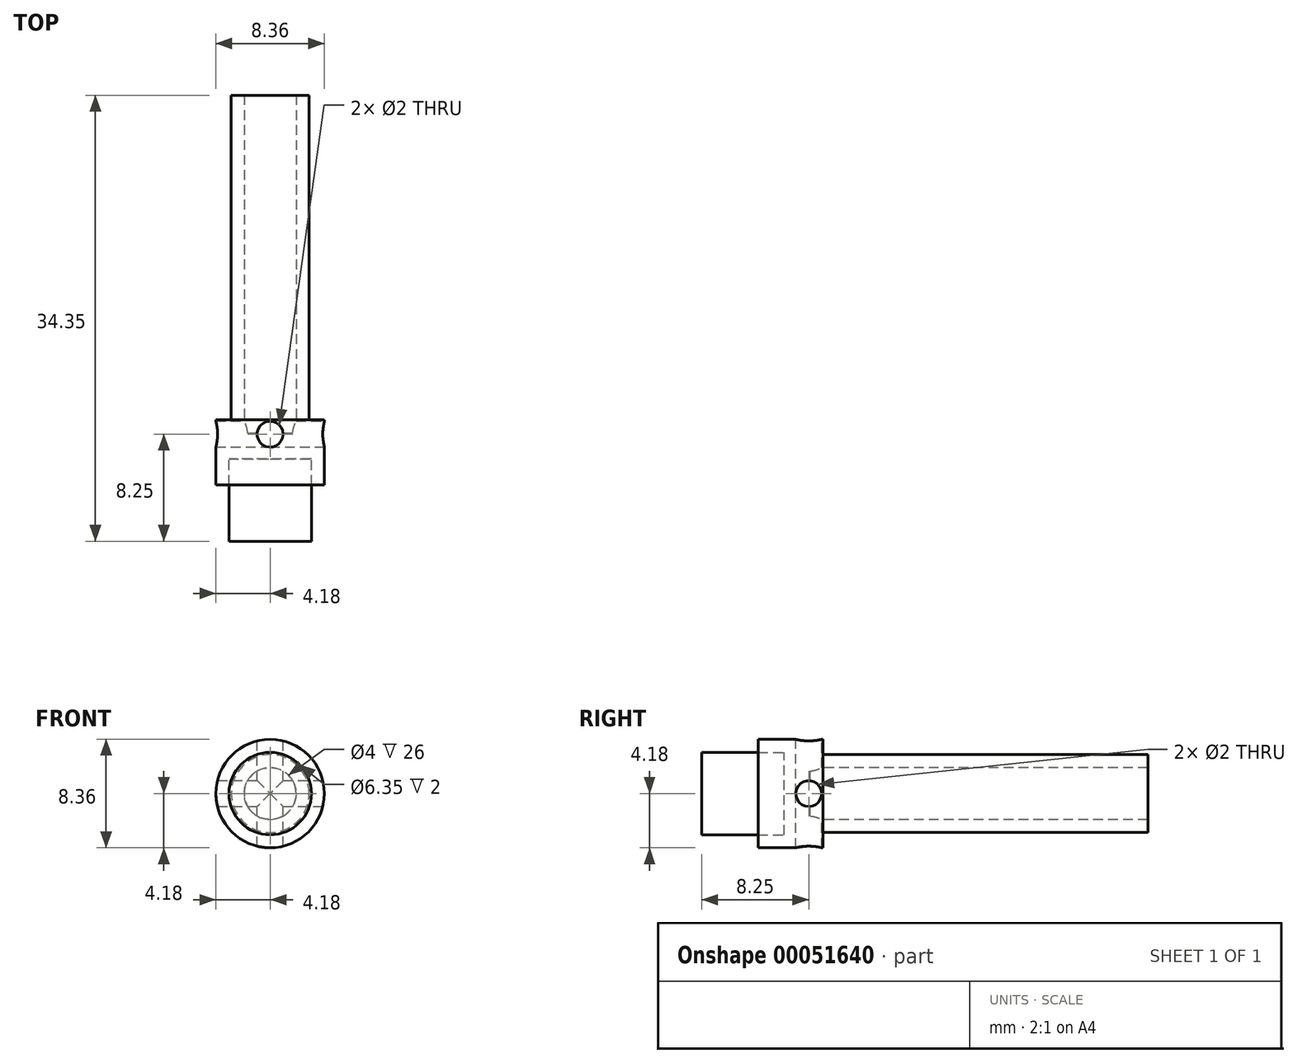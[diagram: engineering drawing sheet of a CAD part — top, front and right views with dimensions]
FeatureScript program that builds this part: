
annotation { "Feature Type Name" : "Feature", "Feature Type Description" : "" }
export const myFeature = defineFeature(function(context is Context, id is Id, definition is map)
    precondition{}
    {
        {
            var Q0;
            Q0=qCreatedBy(makeId("Right.planeOp"),FACE);
            var sketch = newSketch(context, id + "F0", { "sketchPlane" : qUnion([Q0])});
            skLineSegment(sketch, "E0", {"start": v(-30.44, 0) * mm, "end": v(18.55, 0) * mm, "construction": true});
            skLineSegment(sketch, "E1", {"start": v(15, 3) * mm, "end": v(15, 2) * mm});
            skLineSegment(sketch, "E2", {"start": v(15, 2) * mm, "end": v(-11, 2) * mm});
            skLineSegment(sketch, "E3", {"start": v(-13, 3) * mm, "end": v(-13, 0) * mm});
            skLineSegment(sketch, "E4", {"start": v(-13, 0) * mm, "end": v(-11, 0) * mm});
            skLineSegment(sketch, "E5", {"start": v(-11, 0) * mm, "end": v(-11, 2) * mm});
            skArc(sketch, "E6", {"start": v(-5.5, 3) * mm, "mid": v(-5, 2.5) * mm, "end": v(-4.5, 3) * mm, "construction": true});
            skLineSegment(sketch, "E7", {"start": v(-4.5, 3) * mm, "end": v(-5.5, 3) * mm});
            skLineSegment(sketch, "E8", {"start": v(-4.5, 3) * mm, "end": v(2.5, 3) * mm});
            skArc(sketch, "E9", {"start": v(2.5, 3) * mm, "mid": v(3, 2.5) * mm, "end": v(3.5, 3) * mm, "construction": true});
            skLineSegment(sketch, "E10.trimOffspring", {"start": v(3.5, 3) * mm, "end": v(15, 3) * mm});
            skLineSegment(sketch, "E11", {"start": v(-13, 3) * mm, "end": v(-13, 3.18) * mm});
            skLineSegment(sketch, "E12", {"start": v(-10, 3.17) * mm, "end": v(-10, 3) * mm});
            skLineSegment(sketch, "E13", {"start": v(-10, 3) * mm, "end": v(-5.5, 3) * mm});
            skLineSegment(sketch, "E14", {"start": v(-13, 3.17) * mm, "end": v(-15, 3.17) * mm});
            skLineSegment(sketch, "E15", {"start": v(-15, 3.17) * mm, "end": v(-15, 4.17) * mm});
            skLineSegment(sketch, "E16", {"start": v(-15, 4.17) * mm, "end": v(-10, 4.17) * mm});
            skLineSegment(sketch, "E17", {"start": v(-10, 4.17) * mm, "end": v(-10, 3.17) * mm});
            skLineSegment(sketch, "E18", {"start": v(3.5, 3) * mm, "end": v(2.5, 3) * mm});
            skSolve(sketch);
        }
        {
            var Q0;
            Q0=makeQuery(id+"F0.imprint","IMPRINT",FACE,{"disambiguationData":[TD([[makeQuery(id+"F0.imprint","IMPRINT",EDGE,{"derivedFrom":sQuery(id+"F0.wireOp",EDGE,"E1")}),-1.0]])]});
            var Q1;
            {var subQ0=sQuery(id+"F0.wireOp",EDGE,"E11");Q1=makeQuery(id+"F0.imprint","IMPRINT",FACE,{"disambiguationData":[TD([[makeQuery(id+"F0.imprint","IMPRINT",EDGE,{"derivedFrom":subQ0}),-1.0]])]});}
            var Q2;
            Q2=sQuery(id+"F0.wireOp",EDGE,"E0");
            revolve(context, id + "F1", {"entities" : qUnion([Q0, Q1]), "axis" : qUnion([Q2]), "revolveType" : RevolveType.FULL});
        }
        {
            var Q0;
            Q0=qCreatedBy(makeId("Right.planeOp"),FACE);
            var sketch = newSketch(context, id + "F2", { "sketchPlane" : qUnion([Q0])});
            skCircle(sketch, "E19", {"center": v(-11.1, 0) * mm, "radius": 1 * mm});
            skSolve(sketch);
        }
        {
            var Q0;
            Q0 = qSketchRegion(id + "F2", true);
            extrude(context, id + "F3", {"entities" : qUnion([Q0]), "operationType" : NewBodyOperationType.REMOVE, "oppositeDirection" : true, "depth" : 25 * mm, "symmetric" : true});
        }
        {
            var Q0;
            Q0=qCreatedBy(makeId("Top.planeOp"),FACE);
            var sketch = newSketch(context, id + "F4", { "sketchPlane" : qUnion([Q0])});
            skCircle(sketch, "E20", {"center": v(0, -11.1) * mm, "radius": 1 * mm});
            skSolve(sketch);
        }
        {
            var Q0;
            Q0 = qSketchRegion(id + "F4", true);
            extrude(context, id + "F5", {"entities" : qUnion([Q0]), "operationType" : NewBodyOperationType.REMOVE, "oppositeDirection" : true, "depth" : 25 * mm, "symmetric" : true});
        }
        {
            var Q0;
            Q0=makeQuery(id+"F1.opRevolve","SWEPT_FACE",FACE,{"disambiguationData":[OSD([sQuery(id+"F0.wireOp",EDGE,"E3")])]});
            var sketch = newSketch(context, id + "F6", { "sketchPlane" : qUnion([Q0])});
            skCircle(sketch, "E21", {"center": v(0, 0) * mm, "radius": 3.17 * mm});
            skSolve(sketch);
        }
        {
            var Q0;
            Q0 = qSketchRegion(id + "F6", true);
            extrude(context, id + "F7", {"entities" : qUnion([Q0]), "depth" : 6.35 * mm});
        }
    });
